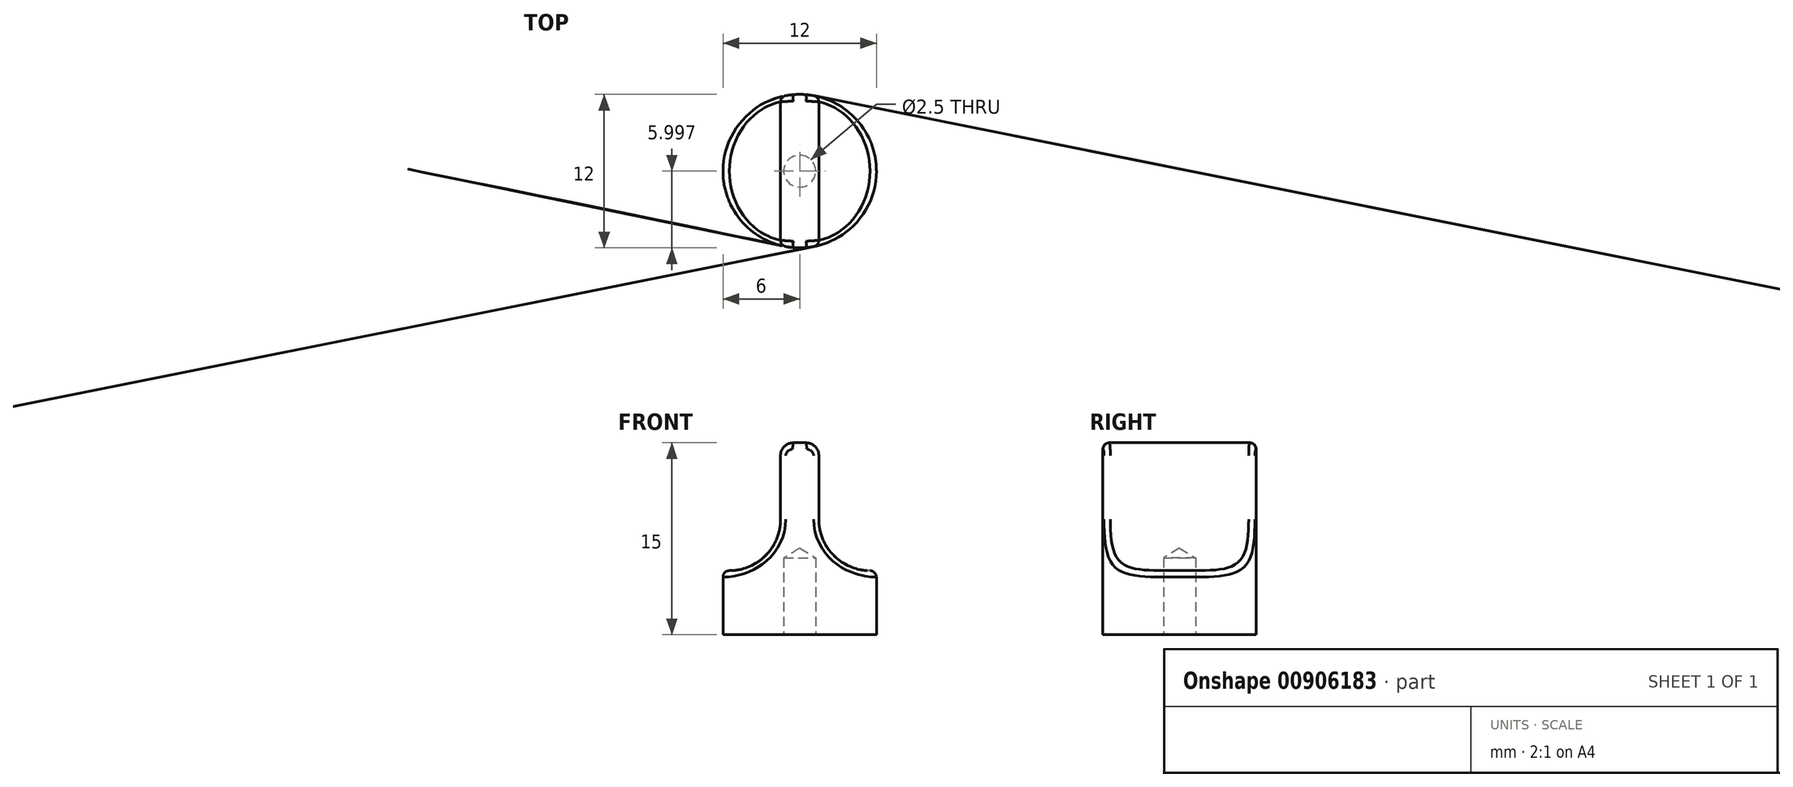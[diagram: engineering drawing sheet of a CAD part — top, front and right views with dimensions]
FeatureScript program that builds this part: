
annotation { "Feature Type Name" : "Feature", "Feature Type Description" : "" }
export const myFeature = defineFeature(function(context is Context, id is Id, definition is map)
    precondition{}
    {
        {
            var Q0;
            Q0=qCreatedBy(makeId("Top.planeOp"),FACE);
            var sketch = newSketch(context, id + "F0", { "sketchPlane" : qUnion([Q0])});
            skCircle(sketch, "E0", {"center": v(-32.66, 35.12) * mm, "radius": 6 * mm});
            skLineSegment(sketch, "E1", {"start": v(-31.16, 35.12) * mm, "end": v(-31.16, 40.93) * mm});
            skLineSegment(sketch, "E2", {"start": v(-31.16, 40.93) * mm, "end": v(-31.16, 29.3) * mm});
            skLineSegment(sketch, "E3", {"start": v(-34.16, 35.12) * mm, "end": v(-34.16, 40.93) * mm});
            skLineSegment(sketch, "E4", {"start": v(-34.16, 40.93) * mm, "end": v(-34.16, 29.3) * mm});
            skSolve(sketch);
        }
        {
            var Q0;
            {var subQ0=sQuery(id+"F0.wireOp",EDGE,"E4");var subQ4=makeQuery(id+"F0.imprint","IMPRINT",VERTEX,{"derivedFrom":subQ0});Q0=makeQuery(id+"F0.imprint","IMPRINT",FACE,{"disambiguationData":[TD([[makeQuery(id+"F0.imprint","IMPRINT",EDGE,{"disambiguationData":[TD([[subQ4,1.0]])],"derivedFrom":subQ0}),-1.0]])]});}
            var Q1;
            {var subQ0=sQuery(id+"F0.wireOp",EDGE,"E2");var subQ3=makeQuery(id+"F0.imprint","IMPRINT",VERTEX,{"derivedFrom":subQ0});Q1=makeQuery(id+"F0.imprint","IMPRINT",FACE,{"disambiguationData":[TD([[makeQuery(id+"F0.imprint","IMPRINT",EDGE,{"disambiguationData":[TD([[subQ3,1.0]])],"derivedFrom":subQ0}),-1.0]])]});}
            var Q2;
            {var subQ0=sQuery(id+"F0.wireOp",EDGE,"E2");var subQ4=makeQuery(id+"F0.imprint","IMPRINT",VERTEX,{"derivedFrom":subQ0});Q2=makeQuery(id+"F0.imprint","IMPRINT",FACE,{"disambiguationData":[TD([[makeQuery(id+"F0.imprint","IMPRINT",EDGE,{"disambiguationData":[TD([[subQ4,1.0]])],"derivedFrom":subQ0}),1.0]])]});}
            extrude(context, id + "F1", {"entities" : qUnion([Q0, Q1, Q2]), "depth" : 5 * mm, "offsetDistance" : 25 * mm});
        }
        {
            var Q0;
            {var subQ0=sQuery(id+"F0.wireOp",EDGE,"E2");var subQ3=makeQuery(id+"F0.imprint","IMPRINT",VERTEX,{"derivedFrom":subQ0});Q0=makeQuery(id+"F0.imprint","IMPRINT",FACE,{"disambiguationData":[TD([[makeQuery(id+"F0.imprint","IMPRINT",EDGE,{"disambiguationData":[TD([[subQ3,1.0]])],"derivedFrom":subQ0}),-1.0]])]});}
            extrude(context, id + "F2", {"entities" : qUnion([Q0]), "operationType" : NewBodyOperationType.ADD, "depth" : 15 * mm, "offsetDistance" : 25 * mm});
        }
        {
            var Q0;
            Q0=makeQuery(id+"F2.boolean.opBoolean","INTERSECT",EDGE,{"derivedFrom":[makeQuery(id+"F1.opExtrude","CAP_FACE",FACE,{"disambiguationData":[OSD([sQuery(id+"F0.wireOp",EDGE,"E0")])],"isStart":false}),makeQuery(id+"F2.opExtrude","SWEPT_FACE",FACE,{"disambiguationData":[OSD([sQuery(id+"F0.wireOp",EDGE,"E4")])]})]});
            var Q1;
            Q1=makeQuery(id+"F2.boolean.opBoolean","INTERSECT",EDGE,{"derivedFrom":[makeQuery(id+"F1.opExtrude","CAP_FACE",FACE,{"disambiguationData":[OSD([sQuery(id+"F0.wireOp",EDGE,"E0")])],"isStart":false}),makeQuery(id+"F2.opExtrude","SWEPT_FACE",FACE,{"disambiguationData":[OSD([sQuery(id+"F0.wireOp",EDGE,"E2")])]})]});
            fillet(context, id + "F3", {"entities" : qUnion([Q0, Q1]), "radius" : 4 * mm, "tangentPropagation" : true, "allowEdgeOverflow" : false});
        }
        {
            var Q0;
            Q0=makeQuery(id+"F2.opExtrude","CAP_EDGE",EDGE,{"disambiguationData":[OSD([sQuery(id+"F0.wireOp",EDGE,"E2")])],"isStart":false});
            var Q1;
            Q1=makeQuery(id+"F2.opExtrude","CAP_EDGE",EDGE,{"disambiguationData":[OSD([sQuery(id+"F0.wireOp",EDGE,"E4")])],"isStart":false});
            fillet(context, id + "F4", {"entities" : qUnion([Q0, Q1]), "radius" : 1 * mm, "tangentPropagation" : true, "allowEdgeOverflow" : false});
        }
        {
            var Q0;
            {var subQ0=sQuery(id+"F0.wireOp",EDGE,"E2");var subQ1=sQuery(id+"F0.wireOp",EDGE,"E0");Q0=makeQuery(id+"F2.opExtrude","SWEPT_EDGE",EDGE,{"disambiguationData":[OSD([subQ1,subQ0]),TDD([makeQuery(id+"F0.imprint","INTERSECT",VERTEX,{"disambiguationData":[OD(0.0)],"derivedFrom":[subQ1,subQ0]})])]});}
            fillet(context, id + "F5", {"entities" : qUnion([Q0]), "radius" : 0.5 * mm, "tangentPropagation" : true, "allowEdgeOverflow" : false});
        }
        {
            var Q0;
            Q0=sQuery(id+"F0.wireOp",VERTEX,"E0.center");
            var Q1;
            Q1=makeQuery(id+"F1.opExtrude","SWEPT_BODY",BODY,{"disambiguationData":[OSD([sQuery(id+"F0.wireOp",EDGE,"E0")])]});
            hole(context, id + "F6", {"style" : HoleStyle.SIMPLE, "endStyle" : HoleEndStyle.BLIND, "oppositeDirection" : true, "standardTappedOrClearance" : lookupTablePath({ "standard" : "ISO", "engagement" : "75%", "pitch" : "0.5 mm", "size" : "M3", "type" : "Tapped" }), "standardBlindInLast" : lookupTablePath({ "standard" : "ISO", "engagement" : "75%", "pitch" : "0.5 mm", "size" : "M3", "type" : "Tapped" }), "holeDiameter" : 2.5 * mm, "majorDiameter" : 3 * mm, "showTappedDepth" : true, "holeDepth" : 6 * mm, "isTappedThrough" : true, "tappedDepth" : 4.5 * mm, "tapClearance" : 3, "startFromSketch" : true, "locations" : qUnion([Q0]), "scope" : qUnion([Q1])});
        }
    });
